# Revit family: Internal block_71_150_DM_1R1A
name_source: partatom
category: Оборудование
units: mm (PartAtom-declared; Revit-internal decimal feet)

## family parameters
Всегда вертикально = Да
Классификация = Нет
На основе рабочей плоскости = Нет
Общий = Нет
При загрузке вырезать с полостями = Нет
Размер круглого соединителя = Использовать диаметр
Тип детали = Нормальный
Точка принадлежности помещению = Нет

## types (6) — shared parameters
00_20_Manufacturer = BLAUBERG
00_20_Name = Internal block
B = 680 мм
Bb = 610 мм
C = 260 мм
Casing Material = Steel, galvanized
E = 515 мм
G = 197 мм
Grid Material = Mesh, steel, painted,  white
Height = 870 мм
I = 207 мм
Length = 1150 мм
Load Classification = HVAC
Maintenance zone material = <По категории>
Maximum Air Flow = 0.0 л/с
Width = 528 мм
dd = 10 мм
dg = 16 мм
dr = 10 мм
ertre = 50 мм
Изготовитель = BLAUBERG
zero-valued in all types: Отметка по умолчанию

## per-type parameters (varying)
| type | A | D | Db | F | H | Power | Weight |
| BLHV-71-I-DM-AC/1R1A | 1209 мм | 1100 мм | 1064 мм | 920 мм | 920 мм | 300 Вт | 33.00 кг |
| BLHV-80-I-DM-AC/1R1A | 1209 мм | 1100 мм | 1064 мм | 920 мм | 920 мм | 300 Вт | 33.00 кг |
| BLHV-90-I-DM-AC/1R1A | 1445 мм | 1337 мм | 1301 мм | 1156 мм | 1156 мм | 340 Вт | 46.00 кг |
| BLHV-100-I-DM-AC/1R1A | 1445 мм | 1337 мм | 1301 мм | 1156 мм | 1156 мм | 340 Вт | 46.00 кг |
| BLHV-120-I-DM-AC/1R1A | 1445 мм | 1337 мм | 1301 мм | 1156 мм | 1156 мм | 340 Вт | 46.00 кг |
| BLHV-150-I-DM-AC/1R1A | 1445 мм | 1337 мм | 1301 мм | 1156 мм | 1156 мм | 340 Вт | 46.00 кг |

note: column(s) folded — value = type name in every type: 00_20_Type
